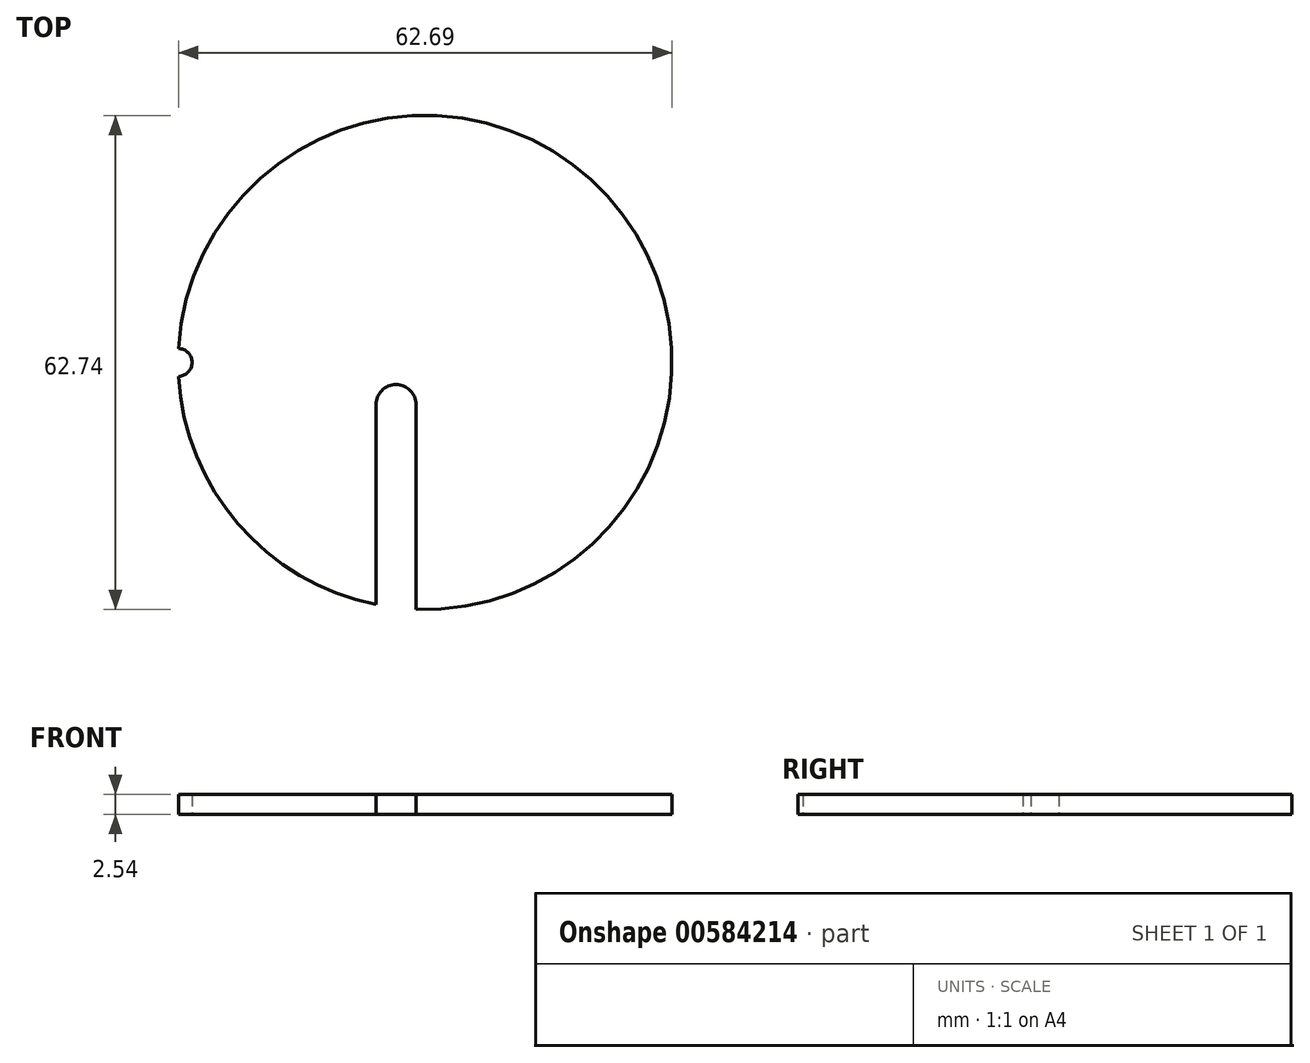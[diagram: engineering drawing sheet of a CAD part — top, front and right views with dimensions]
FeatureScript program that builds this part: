
annotation { "Feature Type Name" : "Feature", "Feature Type Description" : "" }
export const myFeature = defineFeature(function(context is Context, id is Id, definition is map)
    precondition{}
    {
        {
            var Q0;
            Q0=qCreatedBy(makeId("Top.planeOp"),FACE);
            var sketch = newSketch(context, id + "F0", { "sketchPlane" : qUnion([Q0])});
            skArc(sketch, "E0", {"start": v(-31.32, -1.78) * mm, "mid": v(-23.7, -20.54) * mm, "end": v(-6.22, -30.75) * mm});
            skLineSegment(sketch, "E1", {"start": v(-3.68, 41.38) * mm, "end": v(-3.68, -42.39) * mm, "construction": true});
            skLineSegment(sketch, "E2.left", {"start": v(-1.14, -31.35) * mm, "end": v(-1.14, -5.35) * mm});
            skLineSegment(sketch, "E2.right", {"start": v(-6.22, -30.75) * mm, "end": v(-6.22, -5.35) * mm});
            skPoint(sketch, "E2.middle", {"position": v(-3.68, -18.35) * mm});
            skArc(sketch, "E3", {"start": v(-1.14, -5.35) * mm, "mid": v(-3.68, -2.8) * mm, "end": v(-6.22, -5.35) * mm});
            skPoint(sketch, "E4.orphan", {"position": v(-6.22, -31.35) * mm});
            skArc(sketch, "E5", {"start": v(-31.32, -1.78) * mm, "mid": v(-29.6, 0) * mm, "end": v(-31.32, 1.78) * mm});
            skArc(sketch, "E6.trimOffspring", {"start": v(-1.14, -31.35) * mm, "mid": v(23.19, 21.12) * mm, "end": v(-31.32, 1.78) * mm});
            skLineSegment(sketch, "E7", {"start": v(-6.22, -5.35) * mm, "end": v(-1.14, -5.35) * mm, "construction": true});
            skSolve(sketch);
        }
        {
            var Q0;
            Q0 = qSketchRegion(id + "F0", true);
            extrude(context, id + "F1", {"entities" : qUnion([Q0]), "depth" : 2.54 * mm, "offsetDistance" : 25.4 * mm});
        }
    });
